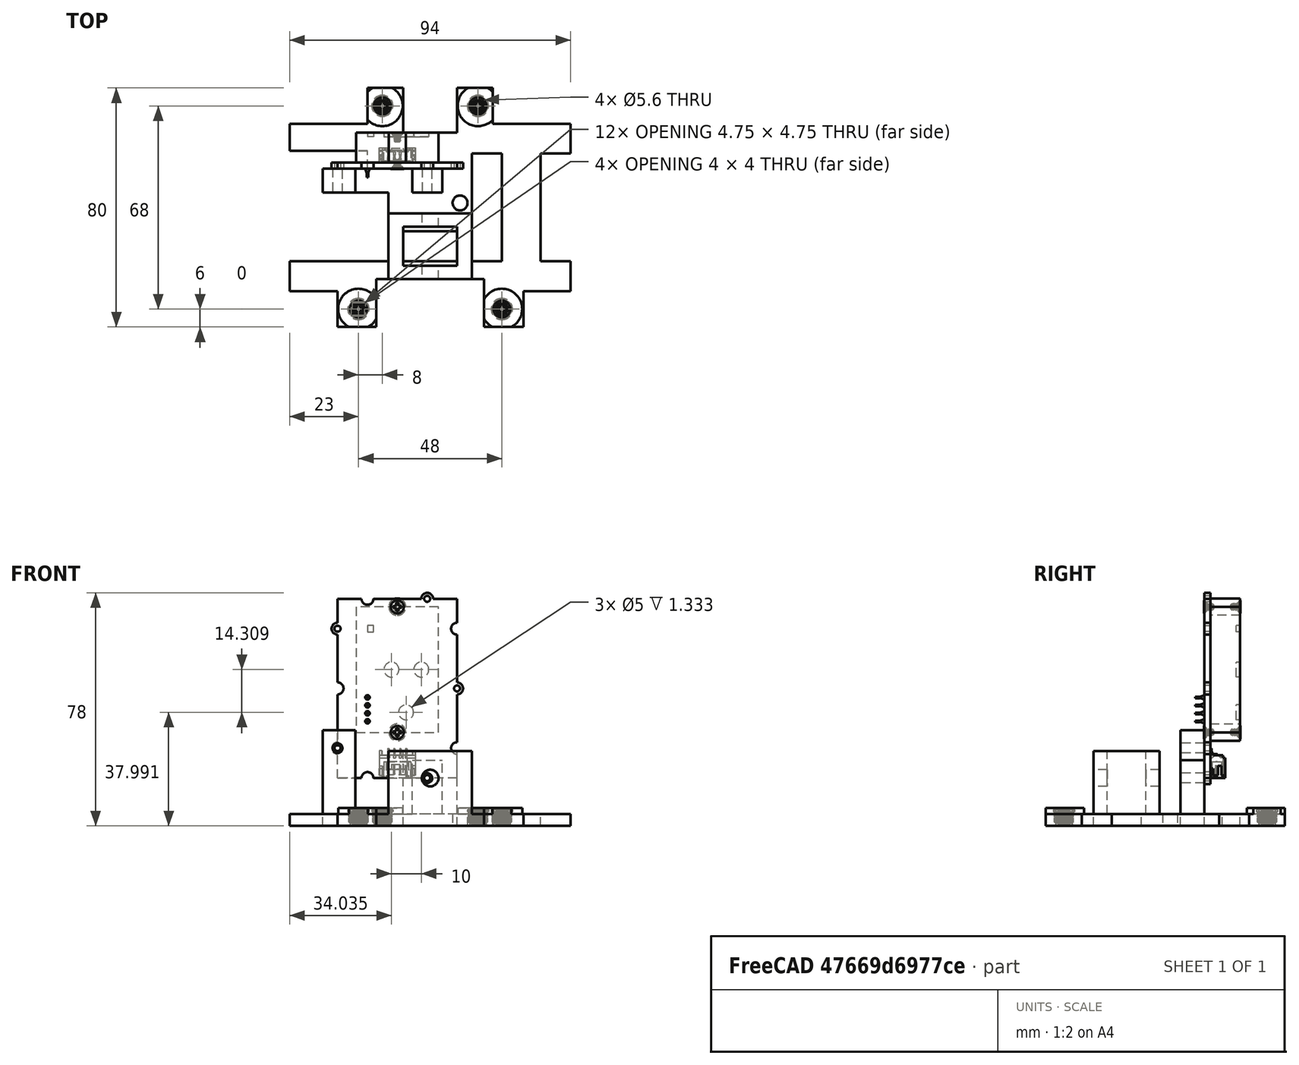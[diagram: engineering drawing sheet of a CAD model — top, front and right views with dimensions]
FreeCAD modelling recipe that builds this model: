
FCSTD DOCUMENT  (FreeCAD 0.20R29177 +233 (Git))
Label: spin09072022
License: All rights reserved
LicenseURL: http://en.wikipedia.org/wiki/All_rights_reserved
objects: Part::Box×23, Part::Cylinder×18, Part::MultiFuse×12, Part::Cut×5, Part::Feature×5
note: 63 computed .brp shape members not serialized (recipe doc carries the construction recipe); baked Part::Feature solids carry a one-line shape summary decoded from their .brp

FEATURE [Part::Cylinder] Cylinder103  label="Cylinder107"
  Angle = 360
  AttacherType = Attacher::AttachEngine3D
  FirstAngle = 0
  Height = 10
  Placement = pos=(63,3,0) rot=(0,0,1;0rad)
  Radius = 2.25
  SecondAngle = 0
FEATURE [Part::Box] Box064  label="base005"
  AttacherType = Attacher::AttachEngine3D
  Height = 4
  Length = 26
  Placement = pos=(-10.25,68,0) rot=(0,0,1;0rad)
  Width = 12
FEATURE [Part::Box] Box060  label="base001"
  AttacherType = Attacher::AttachEngine3D
  Height = 4
  Length = 94
  Width = 80
FEATURE [Part::Box] Box061  label="base002"
  AttacherType = Attacher::AttachEngine3D
  Height = 4
  Length = 26
  Width = 12
FEATURE [Part::Box] Box062  label="base003"
  AttacherType = Attacher::AttachEngine3D
  Height = 4
  Length = 26
  Placement = pos=(68,0,0) rot=(0,0,1;0rad)
  Width = 12
FEATURE [Part::Cylinder] Cylinder104  label="Cylinder103"
  Angle = 360
  AttacherType = Attacher::AttachEngine3D
  FirstAngle = 0
  Height = 10
  Placement = pos=(71,71,0) rot=(0,0,1;0rad)
  Radius = 2.25
  SecondAngle = 0
FEATURE [Part::Cylinder] Cylinder106  label="Cylinder104"
  Angle = 360
  AttacherType = Attacher::AttachEngine3D
  FirstAngle = 0
  Height = 10
  Placement = pos=(23,71,0) rot=(0,0,1;0rad)
  Radius = 2
  SecondAngle = 0
FEATURE [Part::Cylinder] Cylinder105  label="Cylinder108"
  Angle = 360
  AttacherType = Attacher::AttachEngine3D
  FirstAngle = 0
  Height = 10
  Placement = pos=(31,3,0) rot=(0,0,1;0rad)
  Radius = 2.25
  SecondAngle = 0
FEATURE [Part::Box] Box081  label="Cube039"
  AttacherType = Attacher::AttachEngine3D
  Height = 10
  Length = 10
  Placement = pos=(74,26,140) rot=(0,0,1;0rad)
  Width = 36
FEATURE [Part::Box] Box082  label="Cube040"
  AttacherType = Attacher::AttachEngine3D
  Height = 10
  Length = 36
  Placement = pos=(42,1,140) rot=(0,0,1;0rad)
  Width = 19
FEATURE [Part::Box] Box073  label="baseSpineCut"
  AttacherType = Attacher::AttachEngine3D
  Height = 25
  Length = 18
  Placement = pos=(51,26,140) rot=(0,0,1;0rad)
  Width = 10
FEATURE [Part::Cylinder] Cylinder107  label="Cylinder109"
  Angle = 360
  AttacherType = Attacher::AttachEngine3D
  FirstAngle = 0
  Height = 10
  Radius = 1
  SecondAngle = 0
FEATURE [Part::MultiFuse] Fusion123  label="screwIns001"
  Placement = pos=(0,3,0) rot=(0,0,1;0rad)
  Shapes = -> [Cylinder105,Cylinder107,Cylinder103,Cylinder104,Cylinder106]
FEATURE [Part::Box] Box080  label="Cube038"
  AttacherType = Attacher::AttachEngine3D
  Height = 10
  Length = 33
  Placement = pos=(13,26,140) rot=(0,0,1;0rad)
  Width = 23
FEATURE [Part::Box] Box063  label="base004"
  AttacherType = Attacher::AttachEngine3D
  Height = 4
  Length = 26
  Placement = pos=(78,68,0) rot=(0,0,1;0rad)
  Width = 12
FEATURE [Part::MultiFuse] Fusion122
  Shapes = -> [Box064,Box063,Box061,Box062]
FEATURE [Part::Cut] Cut019  label="baseNew"
  Base = -> Box060
  Tool = -> Fusion122
FEATURE [Part::Cut] Cut020  label="baseNew001"
  Base = -> Cut019
  Placement = pos=(107,84,140) rot=(0,0,1;3.14159rad)
  Tool = -> Fusion123
FEATURE [Part::Box] Box083  label="Cube041"
  AttacherType = Attacher::AttachEngine3D
  Height = 25
  Length = 18
  Placement = pos=(51,24.5,144) rot=(0,0,1;0rad)
  Width = 13
FEATURE [Part::Box] Box084  label="Cube042"
  AttacherType = Attacher::AttachEngine3D
  Height = 32
  Length = 40
  Placement = pos=(24,49,140) rot=(0,0,1;0rad)
  Width = 8
FEATURE [Part::Box] Box085  label="Cube043"
  AttacherType = Attacher::AttachEngine3D
  Height = 10
  Length = 15
  Placement = pos=(69,69,140) rot=(0,0,1;1.5708rad)
  Width = 18
FEATURE [Part::Box] Box086  label="baseSpineIn"
  AttacherType = Attacher::AttachEngine3D
  Height = 25
  Length = 28
  Placement = pos=(46,20,140) rot=(0,0,1;0rad)
  Width = 22
FEATURE [Part::Cylinder] Cylinder
  Angle = 360
  AttacherType = Attacher::AttachEngine3D
  FirstAngle = 0
  Height = 50
  Placement = pos=(60,-3,156) rot=(-1,0,0;1.5708rad)
  Radius = 2.8
  SecondAngle = 0
FEATURE [Part::Feature] Feature  label="Seed Grove SCD30"
  Placement = pos=(29,59,156) rot=(0.707107,0,0.707107;3.14159rad)
  shape: bbox 44 x 15.1 x 64 mm, 422 faces, 13 solids (baked)
FEATURE [Part::Cylinder] Cylinder108  label="Cylinder110"
  Angle = 360
  AttacherType = Attacher::AttachEngine3D
  FirstAngle = 0
  Height = 50
  Placement = pos=(80,17,186) rot=(-1,0,0;1.5708rad)
  Radius = 1.65
  SecondAngle = 0
FEATURE [Part::Cylinder] Cylinder109  label="Cylinder111"
  Angle = 360
  AttacherType = Attacher::AttachEngine3D
  FirstAngle = 0
  Height = 50
  Placement = pos=(40,17,166) rot=(-1,0,0;1.5708rad)
  Radius = 1.65
  SecondAngle = 0
FEATURE [Part::Cylinder] Cylinder110  label="Cylinder112"
  Angle = 360
  AttacherType = Attacher::AttachEngine3D
  FirstAngle = 0
  Height = 50
  Placement = pos=(70,17,156) rot=(-1,0,0;1.5708rad)
  Radius = 1.65
  SecondAngle = 0
FEATURE [Part::MultiFuse] Fusion  label="m2Cuts"
  Placement = pos=(-11,30,0) rot=(0,0,1;0rad)
  Shapes = -> [Cylinder108,Cylinder109,Cylinder110]
FEATURE [Part::Box] Box087  label="Cube044"
  AttacherType = Attacher::AttachEngine3D
  Height = 51
  Length = 50
  Placement = pos=(13,49,172) rot=(0,0,1;0rad)
  Width = 8
FEATURE [Part::Box] Box088  label="Cube045"
  AttacherType = Attacher::AttachEngine3D
  Height = 51
  Length = 19
  Placement = pos=(35,49,144) rot=(0,0,1;0rad)
  Width = 8
FEATURE [Part::MultiFuse] Fusion124  label="base"
  Shapes = -> [Cut020,Box084,Box086]
FEATURE [Part::MultiFuse] Fusion125  label="cuts"
  Shapes = -> [Box087,Box088,Fusion,Box085,Box080,Box083,Box082,Box081,Box073,Cylinder]
FEATURE [Part::Box] Box089  label="Cube046"
  AttacherType = Attacher::AttachEngine3D
  Height = 10
  Length = 26
  Placement = pos=(13,57,140) rot=(0,0,1;0rad)
  Width = 6
FEATURE [Part::Feature] Solid  label="m4HeatSet"
  Placement = pos=(36,10,140) rot=(1,0,0;1.5708rad)
  shape: bbox 7.1 x 7.1 x 6.065 mm, 234 faces (baked)
FEATURE [Part::Feature] Solid001  label="m4HeatSet001"
  Placement = pos=(84,10,140) rot=(1,0,0;1.5708rad)
  shape: bbox 7.1 x 7.1 x 6.065 mm, 234 faces (baked)
FEATURE [Part::Feature] Solid002  label="m4HeatSet002"
  Placement = pos=(44,78,140) rot=(1,0,0;1.5708rad)
  shape: bbox 7.1 x 7.1 x 6.065 mm, 234 faces (baked)
FEATURE [Part::Feature] Solid003  label="m4HeatSet003"
  Placement = pos=(76,78,140) rot=(1,0,0;1.5708rad)
  shape: bbox 7.1 x 7.1 x 6.065 mm, 234 faces (baked)
FEATURE [Part::Cylinder] Cylinder111  label="m4HeatSetCut"
  Angle = 360
  AttacherType = Attacher::AttachEngine3D
  FirstAngle = 0
  Height = 10
  Placement = pos=(36,10,140) rot=(0,0,1;0rad)
  Radius = 2.8
  SecondAngle = 0
FEATURE [Part::Cylinder] Cylinder112  label="m4HeatSetCut001"
  Angle = 360
  AttacherType = Attacher::AttachEngine3D
  FirstAngle = 0
  Height = 10
  Placement = pos=(84,10,140) rot=(0,0,1;0rad)
  Radius = 2.8
  SecondAngle = 0
FEATURE [Part::Cylinder] Cylinder113  label="m4HeatSetCut002"
  Angle = 360
  AttacherType = Attacher::AttachEngine3D
  FirstAngle = 0
  Height = 10
  Placement = pos=(76,78,140) rot=(0,0,1;0rad)
  Radius = 2.8
  SecondAngle = 0
FEATURE [Part::Cylinder] Cylinder114  label="m4HeatSetCut003"
  Angle = 360
  AttacherType = Attacher::AttachEngine3D
  FirstAngle = 0
  Height = 10
  Placement = pos=(44,78,140) rot=(0,0,1;0rad)
  Radius = 2.8
  SecondAngle = 0
FEATURE [Part::MultiFuse] Fusion126  label="heatSetCuts"
  Shapes = -> [Cylinder111,Cylinder112,Cylinder113,Cylinder114]
FEATURE [Part::Box] Box091  label="Cube048"
  AttacherType = Attacher::AttachEngine3D
  Height = 10
  Length = 11
  Placement = pos=(13,49,140) rot=(0,0,1;0rad)
  Width = 8
FEATURE [Part::MultiFuse] Fusion127  label="cuts001"
  Shapes = -> [Box091,Fusion126,Box089,Fusion125]
FEATURE [Part::Cylinder] Cylinder115  label="m4HeatSetCut004"
  Angle = 360
  AttacherType = Attacher::AttachEngine3D
  FirstAngle = 0
  Height = 6
  Placement = pos=(36,10,140) rot=(0,0,-1;1.0472rad)
  Radius = 6.8
  SecondAngle = 0
FEATURE [Part::Cylinder] Cylinder116  label="m4HeatSetCut005"
  Angle = 360
  AttacherType = Attacher::AttachEngine3D
  FirstAngle = 0
  Height = 6
  Placement = pos=(84,10,140) rot=(0,0,1;0rad)
  Radius = 6.8
  SecondAngle = 0
FEATURE [Part::Cylinder] Cylinder117  label="m4HeatSetCut006"
  Angle = 360
  AttacherType = Attacher::AttachEngine3D
  FirstAngle = 0
  Height = 6
  Placement = pos=(76,78,140) rot=(0,0,1;0rad)
  Radius = 6.8
  SecondAngle = 0
FEATURE [Part::Cylinder] Cylinder118  label="m4HeatSetCut007"
  Angle = 360
  AttacherType = Attacher::AttachEngine3D
  FirstAngle = 0
  Height = 6
  Placement = pos=(44,78,140) rot=(0,0,1;0rad)
  Radius = 6.8
  SecondAngle = 0
FEATURE [Part::MultiFuse] Fusion128  label="heatSetAddOns"
  Shapes = -> [Cylinder115,Cylinder116,Cylinder117,Cylinder118]
FEATURE [Part::Box] Box092  label="Cube049"
  AttacherType = Attacher::AttachEngine3D
  Height = 10
  Length = 94
  Placement = pos=(13,-4,140) rot=(0,0,1;0rad)
  Width = 8
FEATURE [Part::MultiFuse] Fusion129  label="base006"
  Shapes = -> [Fusion128,Fusion124]
FEATURE [Part::Box] Box093  label="Cube050"
  AttacherType = Attacher::AttachEngine3D
  Height = 10
  Length = 94
  Placement = pos=(13,84,140) rot=(0,0,1;0rad)
  Width = 8
FEATURE [Part::Box] Box094  label="Cube051"
  AttacherType = Attacher::AttachEngine3D
  Height = 10
  Length = 94
  Placement = pos=(89,72,140) rot=(0,0,1;1.5708rad)
  Width = 8
FEATURE [Part::Box] Box095  label="Cube052"
  AttacherType = Attacher::AttachEngine3D
  Height = 10
  Length = 94
  Placement = pos=(39,72,140) rot=(0,0,1;1.5708rad)
  Width = 8
FEATURE [Part::MultiFuse] Fusion130
  Shapes = -> [Box093,Box094,Box095,Box092]
FEATURE [Part::MultiFuse] Fusion131  label="cuts002"
  Shapes = -> [Fusion127,Fusion130]
FEATURE [Part::Box] Box096  label="Cube053"
  AttacherType = Attacher::AttachEngine3D
  Height = 10
  Length = 10
  Placement = pos=(97,26,140) rot=(0,0,1;0rad)
  Width = 36
FEATURE [Part::MultiFuse] Fusion132  label="cuts003"
  Shapes = -> [Fusion131,Box096]
FEATURE [Part::Cut] Cut  label="base007"
  Base = -> Fusion129
  Tool = -> Fusion132
FEATURE [Part::Cylinder] Cylinder119
  Angle = 360
  AttacherType = Attacher::AttachEngine3D
  FirstAngle = 0
  Height = 10
  Placement = pos=(70,45.5,140) rot=(0,0,1;0rad)
  Radius = 2.5
  SecondAngle = 0
FEATURE [Part::Cut] Cut021
  Base = -> Cut
  Tool = -> Cylinder119
FEATURE [Part::Box] Box097  label="Cube054"
  AttacherType = Attacher::AttachEngine3D
  Height = 51
  Length = 19
  Placement = pos=(45,49,162) rot=(0,0,1;0rad)
  Width = 8
FEATURE [Part::Cut] Cut022  label="base008"
  Base = -> Cut021
  Tool = -> Box097
